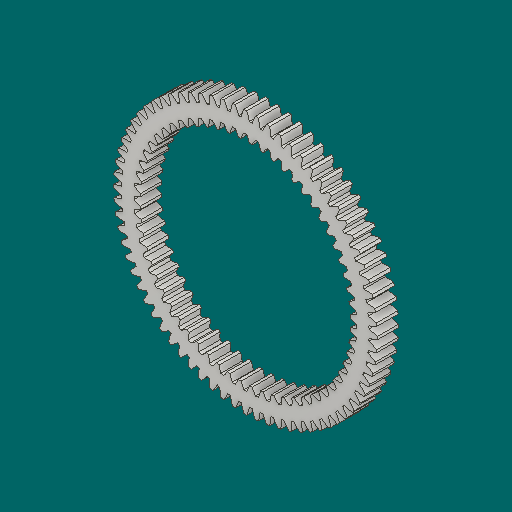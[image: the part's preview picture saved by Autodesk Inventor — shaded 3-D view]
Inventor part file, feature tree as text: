
AUTODESK INVENTOR PART (.ipt)
format: ipt  version: 2023.1 (Build 271208000, 208)  size: 917,504 bytes
history: native  units: in
note: dims shown in document units (in); Inventor stores cm internally (conversion verified against a paired STEP export)
features: other x13, sketch x3, plane x3
ambient origin geometry x8: Origin, YZ Plane, XZ Plane, XY Plane, X Axis, Y Axis, Z Axis, Center Point
bodies: Solid1_1 (feature_tree)
feature tree (19):
  other  "Spur Gear1"
  other  "Solid1::Spur Gear1"
  other  "Solid1_1::Spur Gear1"
  other  "TaggingFeature1"
  sketch  "Sketch1"  dims[d0=0.3937in]
  sketch  "Sketch2"  dims[d9=0.0in]
  sketch  "Sketch3"  dims[d14=0.0in d15=3.6in d16=0.0in d17=0.0in d18=0.0in d19=3.6in]
  plane  "XZ Plane_1"
  plane  "Work Plane2"
  plane  "Work Plane3"
  other  "Srf1"
  other  "Srf1::Derived"
  other  "Start plane iMate"
  other  "Distance iMate"
  other  "Position iMate"
  other  "Mesh iMate"
  other  "Axis iMate"
  other  "Mesh iMate2"
  other  "Align iMate"
